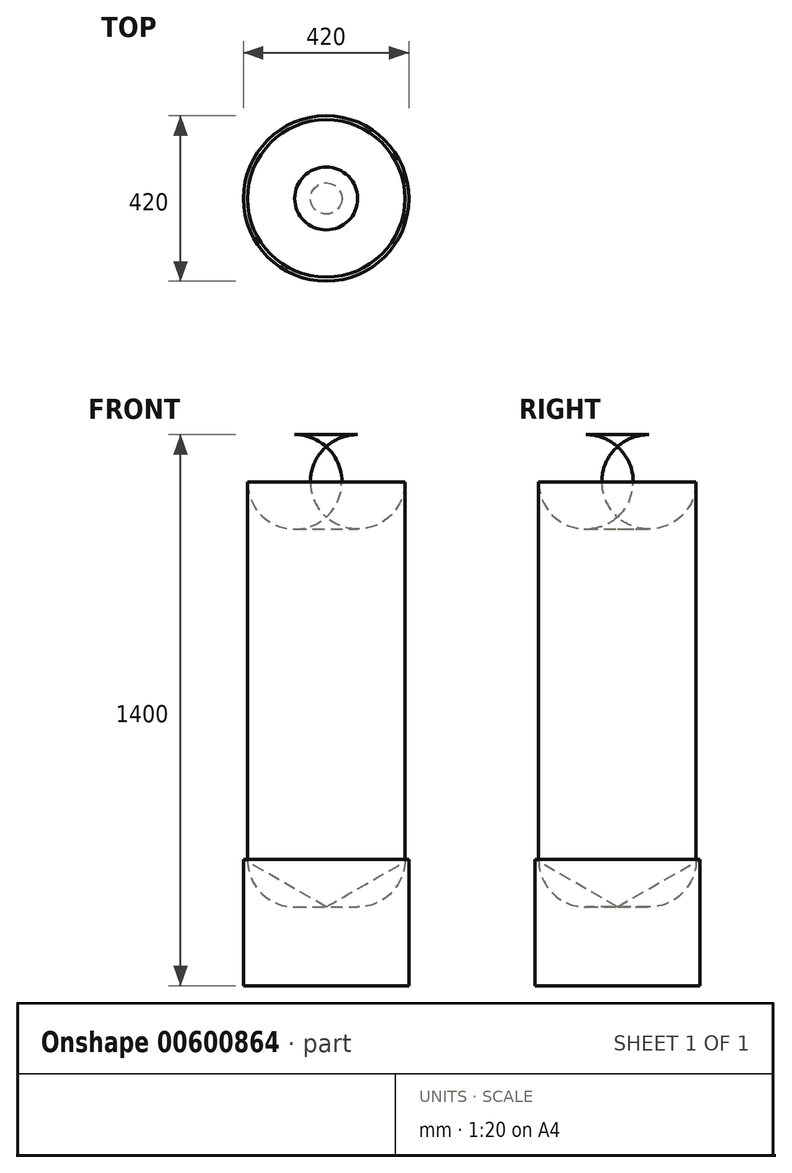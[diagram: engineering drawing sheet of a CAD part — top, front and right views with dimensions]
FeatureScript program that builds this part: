
annotation { "Feature Type Name" : "Feature", "Feature Type Description" : "" }
export const myFeature = defineFeature(function(context is Context, id is Id, definition is map)
    precondition{}
    {
        {
            var Q0;
            Q0=qCreatedBy(makeId("Front.planeOp"),FACE);
            var sketch = newSketch(context, id + "F0", { "sketchPlane" : qUnion([Q0])});
            skLineSegment(sketch, "E0.bottom", {"start": v(0, 0) * mm, "end": v(80, 0) * mm});
            skLineSegment(sketch, "E0.top", {"start": v(0, 1200) * mm, "end": v(80, 1200) * mm});
            skLineSegment(sketch, "E0.left", {"start": v(0, 0) * mm, "end": v(0, 1200) * mm});
            skLineSegment(sketch, "E0.right", {"start": v(200, 120) * mm, "end": v(200, 1080) * mm});
            skPoint(sketch, "E1.visualSharp", {"position": v(200, 1200) * mm});
            skArc(sketch, "E1.filletArc", {"start": v(200, 1080) * mm, "mid": v(164.85, 1164.85) * mm, "end": v(80, 1200) * mm});
            skPoint(sketch, "E2.visualSharp", {"position": v(200, 0) * mm});
            skArc(sketch, "E2.filletArc", {"start": v(80, 0) * mm, "mid": v(164.85, 35.15) * mm, "end": v(200, 120) * mm});
            skSolve(sketch);
        }
        {
            var Q0;
            Q0=makeQuery(id+"F0.imprint","IMPRINT",FACE,{"disambiguationData":[TD([[makeQuery(id+"F0.imprint","IMPRINT",EDGE,{"derivedFrom":sQuery(id+"F0.wireOp",EDGE,"E0.bottom")}),1.0]])]});
            var Q1;
            Q1=sQuery(id+"F0.wireOp",EDGE,"E0.left");
            revolve(context, id + "F1", {"entities" : qUnion([Q0]), "axis" : qUnion([Q1]), "revolveType" : RevolveType.FULL});
        }
        {
            var Q0;
            Q0=qCreatedBy(makeId("Front.planeOp"),FACE);
            var sketch = newSketch(context, id + "F2", { "sketchPlane" : qUnion([Q0])});
            skLineSegment(sketch, "E3", {"start": v(0, 0) * mm, "end": v(0, -200) * mm});
            skLineSegment(sketch, "E4", {"start": v(0, -200) * mm, "end": v(210, -200) * mm});
            skLineSegment(sketch, "E5", {"start": v(210, -200) * mm, "end": v(210, 120.35) * mm});
            skLineSegment(sketch, "E6", {"start": v(210, 120.35) * mm, "end": v(0, 0) * mm});
            skSolve(sketch);
        }
        {
            var Q0;
            Q0=makeQuery(id+"F2.imprint","IMPRINT",FACE,{"disambiguationData":[TD([[makeQuery(id+"F2.imprint","IMPRINT",EDGE,{"derivedFrom":sQuery(id+"F2.wireOp",EDGE,"E3")}),1.0]])]});
            var Q1;
            Q1=sQuery(id+"F2.wireOp",EDGE,"E3");
            revolve(context, id + "F3", {"entities" : qUnion([Q0]), "axis" : qUnion([Q1]), "revolveType" : RevolveType.FULL});
        }
    });
